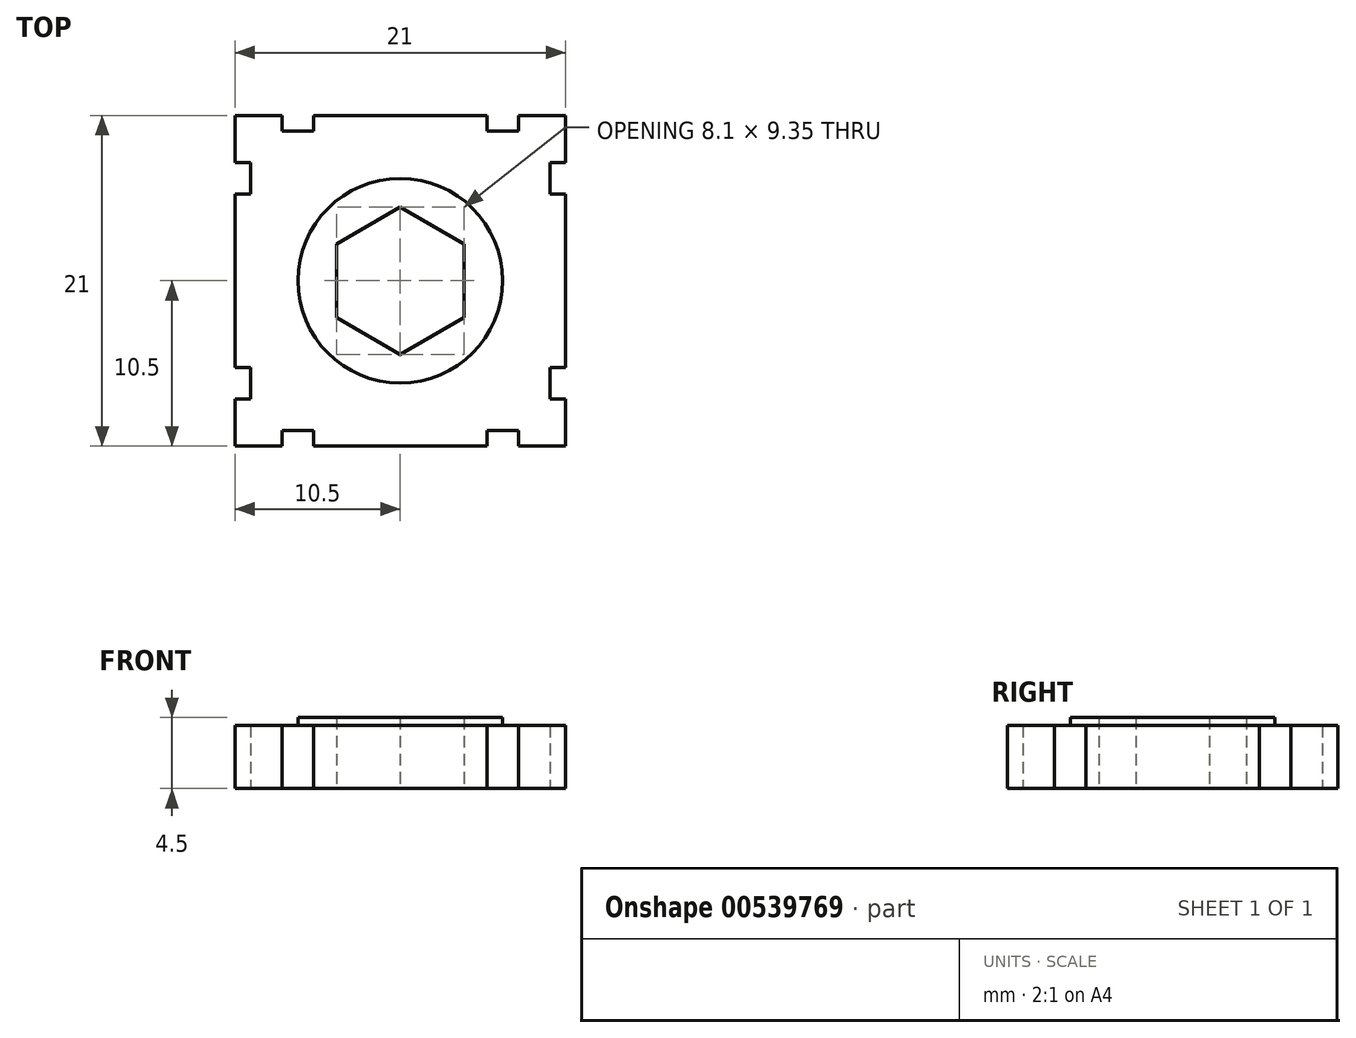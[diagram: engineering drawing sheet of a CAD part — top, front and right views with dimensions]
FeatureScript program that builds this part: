
annotation { "Feature Type Name" : "Feature", "Feature Type Description" : "" }
export const myFeature = defineFeature(function(context is Context, id is Id, definition is map)
    precondition{}
    {
        {
            var Q0;
            Q0=qCreatedBy(makeId("Top.planeOp"),FACE);
            var sketch = newSketch(context, id + "F0", { "sketchPlane" : qUnion([Q0])});
            skCircle(sketch, "E0.cCircle", {"center": v(0, 0) * mm, "radius": 4.05 * mm, "construction": true});
            skLineSegment(sketch, "E0.0", {"start": v(4.05, -2.34) * mm, "end": v(0, -4.68) * mm});
            skLineSegment(sketch, "E0.1", {"start": v(0, -4.68) * mm, "end": v(-4.05, -2.34) * mm});
            skLineSegment(sketch, "E0.2", {"start": v(-4.05, -2.34) * mm, "end": v(-4.05, 2.34) * mm});
            skLineSegment(sketch, "E0.3", {"start": v(-4.05, 2.34) * mm, "end": v(0, 4.68) * mm});
            skLineSegment(sketch, "E0.4", {"start": v(0, 4.68) * mm, "end": v(4.05, 2.34) * mm});
            skLineSegment(sketch, "E0.5", {"start": v(4.05, 2.34) * mm, "end": v(4.05, -2.34) * mm});
            skPoint(sketch, "E0.0.midPoint", {"position": v(2.02, -3.5) * mm});
            skLineSegment(sketch, "E1", {"start": v(0, 0) * mm, "end": v(0, 4.68) * mm, "construction": true});
            skCircle(sketch, "E2", {"center": v(0, 0) * mm, "radius": 6.5 * mm});
            skLineSegment(sketch, "E3.bottom", {"start": v(10.5, -10.5) * mm, "end": v(-10.5, -10.5) * mm});
            skLineSegment(sketch, "E3.top", {"start": v(10.5, 10.5) * mm, "end": v(-10.5, 10.5) * mm});
            skLineSegment(sketch, "E3.left", {"start": v(10.5, -10.5) * mm, "end": v(10.5, 10.5) * mm});
            skLineSegment(sketch, "E3.right", {"start": v(-10.5, -10.5) * mm, "end": v(-10.5, 10.5) * mm});
            skLineSegment(sketch, "E4.bottom", {"start": v(-7.5, 10.5) * mm, "end": v(-5.5, 10.5) * mm});
            skLineSegment(sketch, "E4.top", {"start": v(-7.5, 9.5) * mm, "end": v(-5.5, 9.5) * mm});
            skLineSegment(sketch, "E4.left", {"start": v(-7.5, 10.5) * mm, "end": v(-7.5, 9.5) * mm});
            skLineSegment(sketch, "E4.right", {"start": v(-5.5, 10.5) * mm, "end": v(-5.5, 9.5) * mm});
            skLineSegment(sketch, "E5", {"start": v(-10.5, 10.5) * mm, "end": v(10.5, -10.5) * mm, "construction": true});
            skLineSegment(sketch, "E6.MirrorCS", {"start": v(-10.5, 5.5) * mm, "end": v(-9.5, 5.5) * mm});
            skLineSegment(sketch, "E7.MirrorCS", {"start": v(-9.5, 7.5) * mm, "end": v(-9.5, 5.5) * mm});
            skLineSegment(sketch, "E8.MirrorCS", {"start": v(-10.5, 7.5) * mm, "end": v(-9.5, 7.5) * mm});
            skLineSegment(sketch, "E9.1.0", {"start": v(-10.5, -5.5) * mm, "end": v(-9.5, -5.5) * mm});
            skLineSegment(sketch, "E9.1.1", {"start": v(-9.5, -7.5) * mm, "end": v(-9.5, -5.5) * mm});
            skLineSegment(sketch, "E9.1.2", {"start": v(-10.5, -7.5) * mm, "end": v(-9.5, -7.5) * mm});
            skLineSegment(sketch, "E9.1.3", {"start": v(-7.5, -10.5) * mm, "end": v(-7.5, -9.5) * mm});
            skLineSegment(sketch, "E9.1.4", {"start": v(-7.5, -9.5) * mm, "end": v(-5.5, -9.5) * mm});
            skLineSegment(sketch, "E9.1.5", {"start": v(-5.5, -10.5) * mm, "end": v(-5.5, -9.5) * mm});
            skLineSegment(sketch, "E9.2.0", {"start": v(5.5, -10.5) * mm, "end": v(5.5, -9.5) * mm});
            skLineSegment(sketch, "E9.2.1", {"start": v(7.5, -9.5) * mm, "end": v(5.5, -9.5) * mm});
            skLineSegment(sketch, "E9.2.2", {"start": v(7.5, -10.5) * mm, "end": v(7.5, -9.5) * mm});
            skLineSegment(sketch, "E9.2.3", {"start": v(10.5, -7.5) * mm, "end": v(9.5, -7.5) * mm});
            skLineSegment(sketch, "E9.2.4", {"start": v(9.5, -7.5) * mm, "end": v(9.5, -5.5) * mm});
            skLineSegment(sketch, "E9.2.5", {"start": v(10.5, -5.5) * mm, "end": v(9.5, -5.5) * mm});
            skLineSegment(sketch, "E9.3.0", {"start": v(10.5, 5.5) * mm, "end": v(9.5, 5.5) * mm});
            skLineSegment(sketch, "E9.3.1", {"start": v(9.5, 7.5) * mm, "end": v(9.5, 5.5) * mm});
            skLineSegment(sketch, "E9.3.2", {"start": v(10.5, 7.5) * mm, "end": v(9.5, 7.5) * mm});
            skLineSegment(sketch, "E9.3.3", {"start": v(7.5, 10.5) * mm, "end": v(7.5, 9.5) * mm});
            skLineSegment(sketch, "E9.3.4", {"start": v(7.5, 9.5) * mm, "end": v(5.5, 9.5) * mm});
            skLineSegment(sketch, "E9.3.5", {"start": v(5.5, 10.5) * mm, "end": v(5.5, 9.5) * mm});
            skSolve(sketch);
        }
        {
            var Q0;
            Q0=makeQuery(id+"F0.imprint","IMPRINT",FACE,{"disambiguationData":[TD([[makeQuery(id+"F0.imprint","IMPRINT",EDGE,{"derivedFrom":sQuery(id+"F0.wireOp",EDGE,"E2")}),-1.0]])]});
            extrude(context, id + "F1", {"entities" : qUnion([Q0]), "depth" : 4 * mm, "offsetDistance" : 25 * mm});
        }
        {
            var Q0;
            Q0=makeQuery(id+"F0.imprint","IMPRINT",FACE,{"disambiguationData":[TD([[makeQuery(id+"F0.imprint","IMPRINT",EDGE,{"derivedFrom":sQuery(id+"F0.wireOp",EDGE,"E0.0")}),1.0]])]});
            extrude(context, id + "F2", {"entities" : qUnion([Q0]), "operationType" : NewBodyOperationType.ADD, "depth" : 4.5 * mm, "offsetDistance" : 25 * mm});
        }
    });
